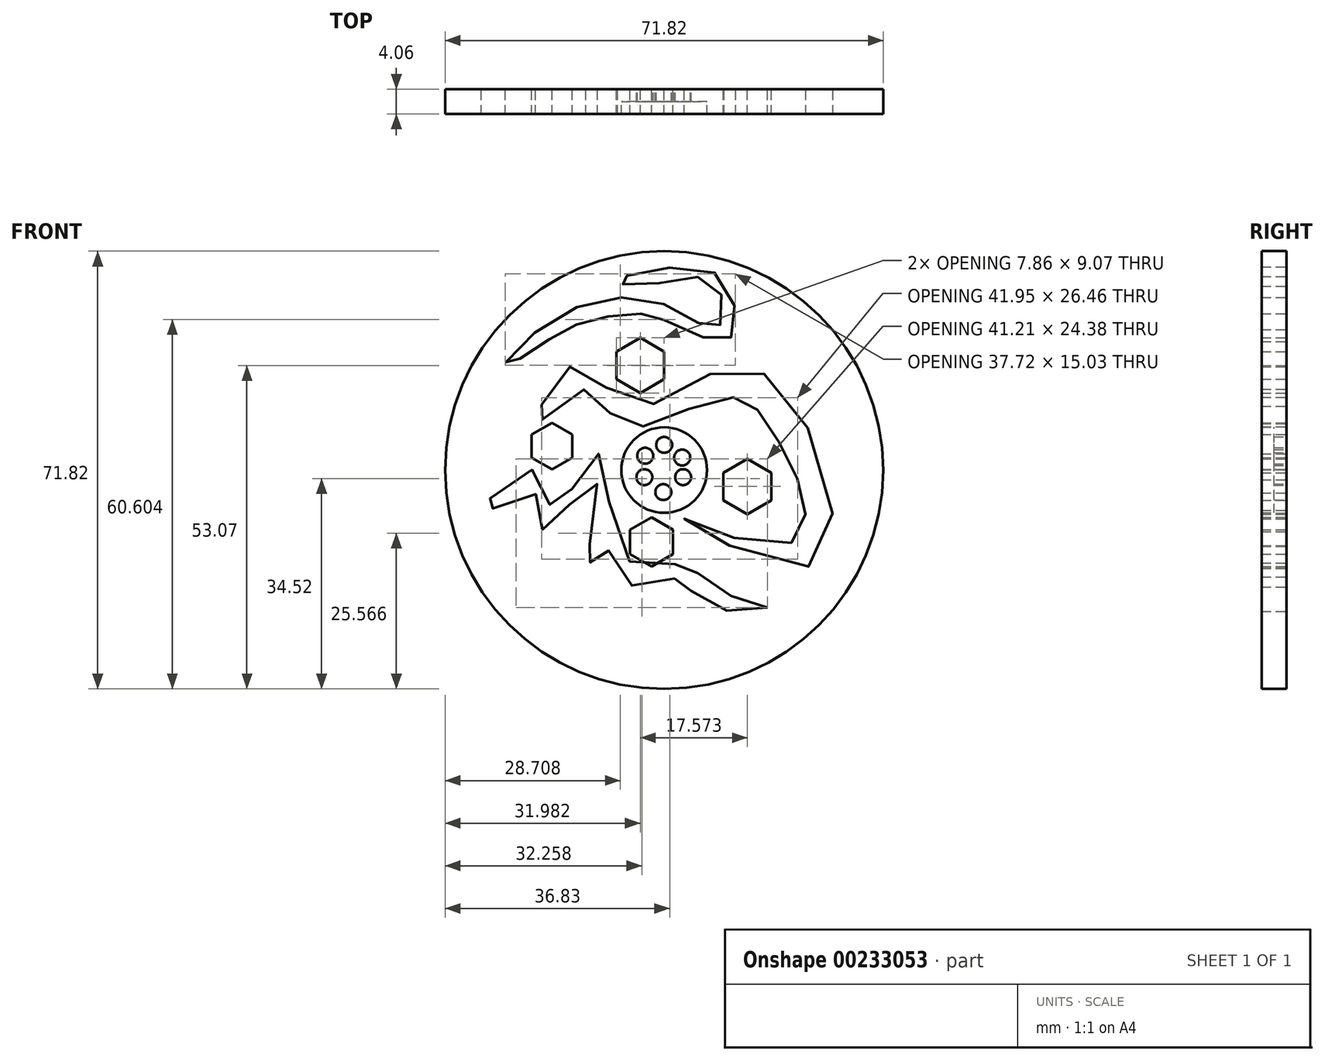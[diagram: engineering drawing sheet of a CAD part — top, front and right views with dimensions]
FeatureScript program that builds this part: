
annotation { "Feature Type Name" : "Feature", "Feature Type Description" : "" }
export const myFeature = defineFeature(function(context is Context, id is Id, definition is map)
    precondition{}
    {
        {
            var Q0;
            Q0=qCreatedBy(makeId("Front.planeOp"),FACE);
            var sketch = newSketch(context, id + "F0", { "sketchPlane" : qUnion([Q0])});
            skCircle(sketch, "E0", {"center": v(0, 0) * mm, "radius": 35.9 * mm});
            skFitSpline(sketch, "E1", {"points": [v(-20.05, 10.75) * mm, v(-14.27, 17.16) * mm, v(-4.96, 10.54) * mm, v(10.34, 16.75) * mm, v(23.16, 7.65) * mm, v(24.19, -15.71) * mm, v(3.3, -8.06) * mm, v(16.33, -12.4) * mm, v(22.95, -9.72) * mm, v(22.54, -4.13) * mm, v(20.47, 1.86) * mm, v(15.92, 8.9) * mm, v(13.85, 11.37) * mm, v(7.44, 11.37) * mm, v(-3.1, 7.24) * mm, v(-8.68, 9.1) * mm, v(-13.02, 13.23) * mm, v(-20.88, 7.65) * mm, v(-20.05, 10.75) * mm]});
            skCircle(sketch, "E2", {"center": v(0, 0) * mm, "radius": 7.02 * mm});
            skCircle(sketch, "E3", {"center": v(0, 4.13) * mm, "radius": 1.3 * mm});
            skCircle(sketch, "E4", {"center": v(2.96, 2.06) * mm, "radius": 1.3 * mm});
            skCircle(sketch, "E5", {"center": v(3.1, -1.16) * mm, "radius": 1.3 * mm});
            skCircle(sketch, "E6", {"center": v(-0.15, -3.6) * mm, "radius": 1.3 * mm});
            skCircle(sketch, "E7", {"center": v(-3.1, 2.35) * mm, "radius": 1.3 * mm});
            skCircle(sketch, "E8", {"center": v(-3.25, -1.16) * mm, "radius": 1.3 * mm});
            skFitSpline(sketch, "E9", {"points": [v(16.95, -22.54) * mm, v(6.82, -18.81) * mm, v(4.34, -15.3) * mm, v(-6, -14.68) * mm, v(-10.96, 2.69) * mm, v(-17.99, -6.62) * mm, v(-21.5, 0) * mm, v(-29.98, -7.03) * mm, v(-21.09, -3.93) * mm, v(-19.64, -10.13) * mm, v(-11.37, -1.65) * mm, v(-12.82, -16.13) * mm, v(-10.13, -12.4) * mm, v(-5.58, -18.81) * mm, v(3.51, -17.57) * mm, v(5.58, -21.7) * mm, v(16.95, -22.54) * mm]});
            skCircle(sketch, "E10.cCircle", {"center": v(13.65, -2.69) * mm, "radius": 3.93 * mm, "construction": true});
            skLineSegment(sketch, "E10.0", {"start": v(17.57, -0.42) * mm, "end": v(17.57, -4.96) * mm});
            skLineSegment(sketch, "E10.1", {"start": v(17.57, -4.96) * mm, "end": v(13.65, -7.22) * mm});
            skLineSegment(sketch, "E10.2", {"start": v(13.65, -7.22) * mm, "end": v(9.72, -4.96) * mm});
            skLineSegment(sketch, "E10.3", {"start": v(9.72, -4.96) * mm, "end": v(9.72, -0.42) * mm});
            skLineSegment(sketch, "E10.4", {"start": v(9.72, -0.42) * mm, "end": v(13.65, 1.85) * mm});
            skLineSegment(sketch, "E10.5", {"start": v(13.65, 1.85) * mm, "end": v(17.57, -0.42) * mm});
            skPoint(sketch, "E10.0.midPoint", {"position": v(17.57, -2.69) * mm});
            skCircle(sketch, "E11.cCircle", {"center": v(-18.4, 3.93) * mm, "radius": 3.3 * mm, "construction": true});
            skLineSegment(sketch, "E11.0", {"start": v(-15.1, 5.84) * mm, "end": v(-15.1, 2.02) * mm});
            skLineSegment(sketch, "E11.1", {"start": v(-15.1, 2.02) * mm, "end": v(-18.4, 0.1) * mm});
            skLineSegment(sketch, "E11.2", {"start": v(-18.4, 0.1) * mm, "end": v(-21.7, 2.02) * mm});
            skLineSegment(sketch, "E11.3", {"start": v(-21.7, 2.02) * mm, "end": v(-21.7, 5.84) * mm});
            skLineSegment(sketch, "E11.4", {"start": v(-21.7, 5.84) * mm, "end": v(-18.4, 7.75) * mm});
            skLineSegment(sketch, "E11.5", {"start": v(-18.4, 7.75) * mm, "end": v(-15.1, 5.84) * mm});
            skPoint(sketch, "E11.0.midPoint", {"position": v(-15.1, 3.93) * mm});
            skCircle(sketch, "E12.cCircle", {"center": v(-2.07, -11.78) * mm, "radius": 3.51 * mm, "construction": true});
            skLineSegment(sketch, "E12.0", {"start": v(1.45, -9.76) * mm, "end": v(1.45, -13.81) * mm});
            skLineSegment(sketch, "E12.1", {"start": v(1.45, -13.81) * mm, "end": v(-2.07, -15.84) * mm});
            skLineSegment(sketch, "E12.2", {"start": v(-2.07, -15.84) * mm, "end": v(-5.58, -13.81) * mm});
            skLineSegment(sketch, "E12.3", {"start": v(-5.58, -13.81) * mm, "end": v(-5.58, -9.76) * mm});
            skLineSegment(sketch, "E12.4", {"start": v(-5.58, -9.76) * mm, "end": v(-2.07, -7.73) * mm});
            skLineSegment(sketch, "E12.5", {"start": v(-2.07, -7.73) * mm, "end": v(1.45, -9.76) * mm});
            skPoint(sketch, "E12.0.midPoint", {"position": v(1.45, -11.78) * mm});
            skCircle(sketch, "E13.cCircle", {"center": v(-3.93, 17.16) * mm, "radius": 3.93 * mm, "construction": true});
            skLineSegment(sketch, "E13.0", {"start": v(0, 19.43) * mm, "end": v(0, 14.9) * mm});
            skLineSegment(sketch, "E13.1", {"start": v(0, 14.9) * mm, "end": v(-3.93, 12.62) * mm});
            skLineSegment(sketch, "E13.2", {"start": v(-3.93, 12.62) * mm, "end": v(-7.86, 14.9) * mm});
            skLineSegment(sketch, "E13.3", {"start": v(-7.86, 14.9) * mm, "end": v(-7.86, 19.43) * mm});
            skLineSegment(sketch, "E13.4", {"start": v(-7.86, 19.43) * mm, "end": v(-3.93, 21.7) * mm});
            skLineSegment(sketch, "E13.5", {"start": v(-3.93, 21.7) * mm, "end": v(0, 19.43) * mm});
            skPoint(sketch, "E13.0.midPoint", {"position": v(0, 17.16) * mm});
            skFitSpline(sketch, "E14", {"points": [v(0, 24.6) * mm, v(9.51, 21.09) * mm, v(11.58, 23.36) * mm, v(9.1, 31.84) * mm, v(-3.51, 32.46) * mm, v(-7.65, 31.01) * mm, v(-3.51, 30.18) * mm, v(6, 31.63) * mm, v(9.72, 27.5) * mm, v(8.48, 23.16) * mm, v(3.3, 25.64) * mm, v(-7.44, 28.32) * mm, v(-20.47, 23.16) * mm, v(-26.05, 17.16) * mm, v(-22.12, 19.23) * mm, v(-16.33, 22.95) * mm, v(-10.34, 25.02) * mm, v(-3.51, 25.64) * mm, v(0, 24.6) * mm]});
            skSolve(sketch);
        }
        {
            var Q0;
            Q0=makeQuery(id+"F0.imprint","IMPRINT",FACE,{"disambiguationData":[TD([[makeQuery(id+"F0.imprint","IMPRINT",EDGE,{"derivedFrom":sQuery(id+"F0.wireOp",EDGE,"E0")}),1.0]])]});
            extrude(context, id + "F1", {"entities" : qUnion([Q0]), "depth" : 4.06 * mm});
        }
        {
            var Q0;
            Q0=makeQuery(id+"F0.imprint","IMPRINT",FACE,{"disambiguationData":[TD([[makeQuery(id+"F0.imprint","IMPRINT",EDGE,{"derivedFrom":sQuery(id+"F0.wireOp",EDGE,"E2")}),1.0]])]});
            extrude(context, id + "F2", {"entities" : qUnion([Q0]), "operationType" : NewBodyOperationType.ADD, "depth" : 2.03 * mm});
        }
        {
            var Q0;
            Q0 = qSketchRegion(id + "F0", true);
            extrude(context, id + "F3", {"entities" : qUnion([Q0]), "operationType" : NewBodyOperationType.ADD, "depth" : 1.02 * mm});
        }
    });
